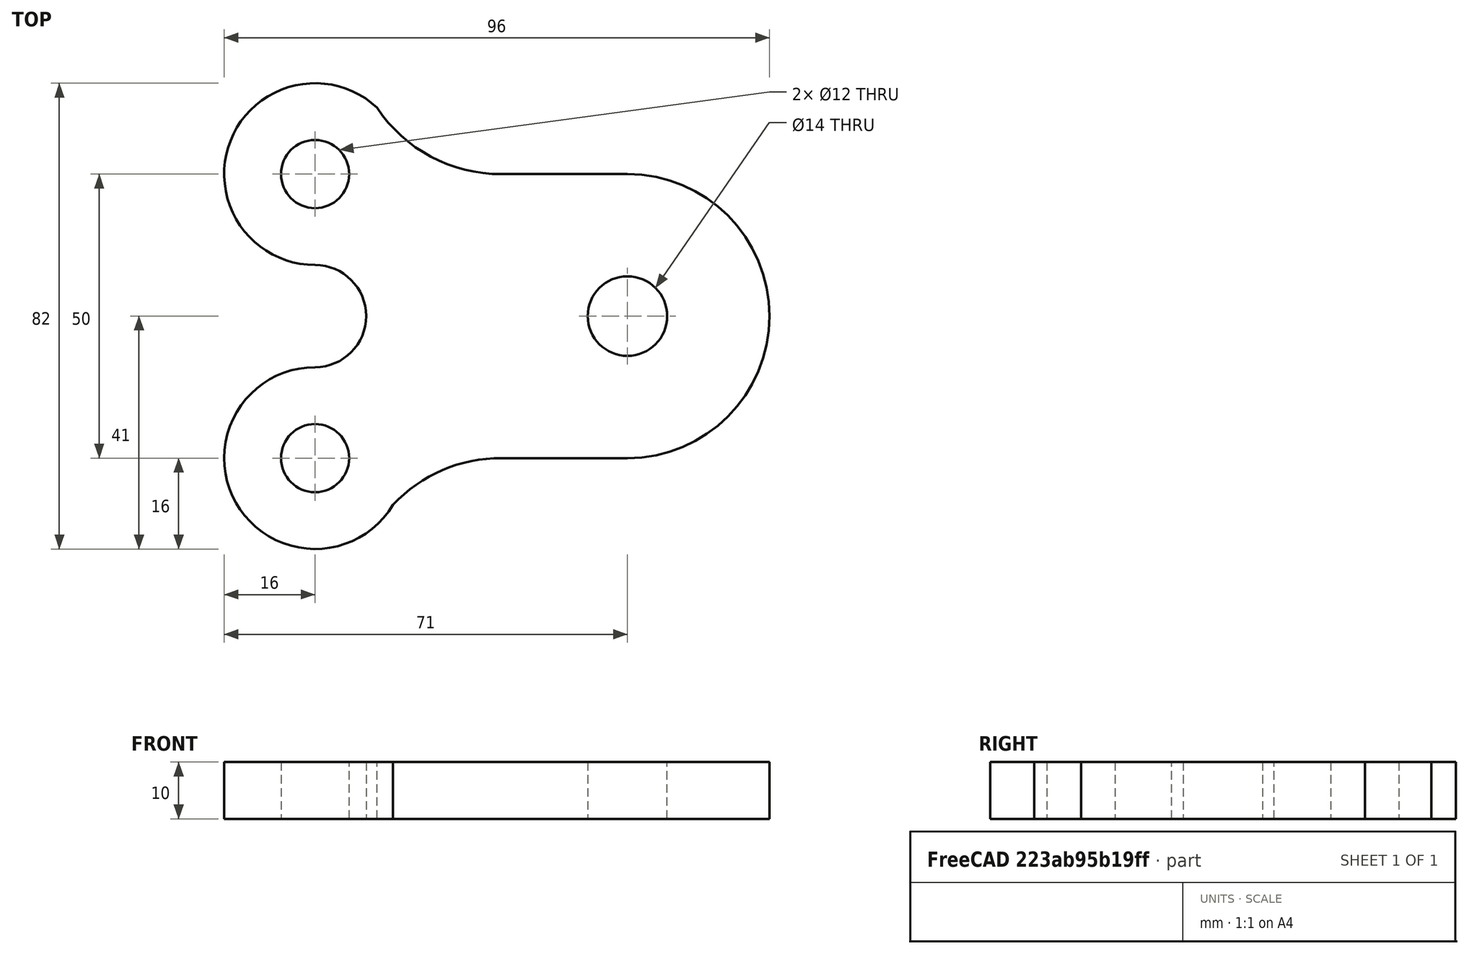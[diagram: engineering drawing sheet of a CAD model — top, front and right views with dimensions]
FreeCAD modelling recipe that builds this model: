
FCSTD DOCUMENT  (FreeCAD 0.18R4 (GitTag))
Label: Template 3 D39
License: All rights reserved
LicenseURL: http://en.wikipedia.org/wiki/All_rights_reserved
objects: TechDraw::DrawViewDimension×21, TechDraw::DrawProjGroupItem×8, TechDraw::DrawProjGroup×5, TechDraw::DrawViewAnnotation×4, TechDraw::DrawSVGTemplate×3, TechDraw::DrawPage×3, Sketcher::SketchObject×1, PartDesign::Pad×1, PartDesign::Body×1
note: 4 computed .brp shape members not serialized (recipe doc carries the construction recipe); baked Part::Feature solids carry a one-line shape summary decoded from their .brp

FEATURE [Sketcher::SketchObject] Sketch
  MapMode = 5
  Support = -> [XY_Plane]
  constraints (32):
    c: Perpendicular(g1,g-2) = 4.71239
    c: Perpendicular(g0,g-2) = 4.71239
    c: Coincident(g2,g0)
    c: Coincident(g2,g1)
    c: Radius(g2) = 25
    c: Coincident(g2,g-1)
    c: Coincident(g3,g2)
    c: Diameter(g3) = 14
    c: DistanceY(g5,g4) = 50
    c: Diameter(g4) = 12
    c: Diameter(g5) = 12
    c: Coincident(g6,g4)
    c: Coincident(g7,g5)
    c: Radius(g6) = 16
    c: Radius(g7) = 16
    c: PointOnObject(g8,g-1)
    c: Coincident(g8,g6)
    c: Coincident(g8,g7)
    c: Radius(g8) = 9
    c: Distance(g4,g0) = 55
    c: Distance(g5,g1) = 55
    c: DistanceX(g-2,g6) = -55
    c: DistanceX(g-2,g7) = -55
    c: Distance(g0,g1) = 50
    c: Coincident(g10,g0)
    c: Coincident(g10,g6)
    c: Coincident(g1,g9)
    c: Coincident(g9,g7)
    c: Radius(g10) = 26
    c: Radius(g9) = 26
    c: DistanceX(g0,g0) = 22.18
    c: DistanceY(g7,g6) = 69.89
FEATURE [PartDesign::Pad] Pad
  Length = 10
  Length2 = 100
  Profile = -> Sketch
  Type = 0
FEATURE [PartDesign::Body] Body
  Group = -> [Sketch,Pad]
  Origin = -> Origin
  Tip = -> Pad
FEATURE [TechDraw::DrawSVGTemplate] Template
  EditableTexts = Designed_by_Name=D 39; Drawing_number=AOT; FC-Date=19/12/2021; FC-SC=Scale; FC-SH=Sheet; FC-Title=Template 3; Subtitle=AKASHDIP MAHAPATRA; Weight=Weight
  Height = 210
  Orientation = 1
  Width = 297
FEATURE [TechDraw::DrawProjGroupItem] ProjItem  label="Front"
  CoarseView = false
  Direction = (0.41,-0.709,0.574)
  Focus = 100
  HardHidden = false
  IsoCount = 0
  IsoHidden = false
  IsoVisible = false
  LockPosition = true
  Perspective = false
  Rotation = 0
  RotationVector = (0.866,0.5,0)
  ScaleType = 2
  SeamHidden = false
  SeamVisible = true
  SmoothHidden = false
  SmoothVisible = true
  Source = -> [Pad]
  Type = 0
  X = 0
  Y = 0
FEATURE [TechDraw::DrawProjGroup] ProjGroup
  Anchor = -> ProjItem
  AutoDistribute = true
  LockPosition = false
  ProjectionType = 0
  Rotation = 0
  ScaleType = 0
  Source = -> [Pad]
  Views = -> [ProjItem]
  X = 0
  Y = 0
  spacingX = 15
  spacingY = 15
FEATURE [TechDraw::DrawProjGroupItem] ProjItem001  label="Front001"
  CoarseView = false
  Direction = (0,0,1)
  Focus = 100
  HardHidden = false
  IsoCount = 0
  IsoHidden = false
  IsoVisible = false
  LockPosition = true
  Perspective = false
  Rotation = 0
  RotationVector = (1,0,0)
  ScaleType = 2
  SeamHidden = false
  SeamVisible = true
  SmoothHidden = false
  SmoothVisible = true
  Source = -> [Pad]
  Type = 0
  X = 0
  Y = 0
FEATURE [TechDraw::DrawProjGroupItem] ProjItem002  label="Bottom"
  CoarseView = false
  Direction = (0,-1,0)
  Focus = 100
  HardHidden = false
  IsoCount = 0
  IsoHidden = false
  IsoVisible = false
  LockPosition = false
  Perspective = false
  Rotation = 0
  RotationVector = (1,0,0)
  ScaleType = 2
  SeamHidden = false
  SeamVisible = true
  SmoothHidden = false
  SmoothVisible = true
  Source = -> [Pad]
  Type = 5
  X = 0
  Y = 97
FEATURE [TechDraw::DrawProjGroupItem] ProjItem004  label="Right"
  CoarseView = false
  Direction = (1,0,1e-16)
  Focus = 100
  HardHidden = false
  IsoCount = 0
  IsoHidden = false
  IsoVisible = false
  LockPosition = false
  Perspective = false
  Rotation = 0
  RotationVector = (1,0,0)
  ScaleType = 2
  SeamHidden = false
  SeamVisible = true
  SmoothHidden = false
  SmoothVisible = true
  Source = -> [Pad]
  Type = 2
  X = 0
  Y = 0
FEATURE [TechDraw::DrawProjGroupItem] ProjItem005  label="Left"
  CoarseView = false
  Direction = (-1,0,1e-16)
  Focus = 100
  HardHidden = false
  IsoCount = 0
  IsoHidden = false
  IsoVisible = false
  LockPosition = false
  Perspective = false
  Rotation = 0
  RotationVector = (1,0,0)
  ScaleType = 2
  SeamHidden = false
  SeamVisible = true
  SmoothHidden = false
  SmoothVisible = true
  Source = -> [Pad]
  Type = 1
  X = 0
  Y = 0
FEATURE [TechDraw::DrawProjGroup] ProjGroup001
  Anchor = -> ProjItem001
  AutoDistribute = true
  LockPosition = false
  ProjectionType = 0
  Rotation = 0
  ScaleType = 0
  Source = -> [Pad]
  Views = -> [ProjItem001,ProjItem002,ProjItem004,ProjItem005]
  X = 0
  Y = 0
  spacingX = 15
  spacingY = 15
FEATURE [TechDraw::DrawViewDimension] Dimension
  Arbitrary = false
  FormatSpec = R%.2f
  LockPosition = false
  MeasureType = 1
  OverTolerance = 0
  References2D = -> [ProjItem001]
  Rotation = 0
  ScaleType = 0
  Type = 4
  UnderTolerance = 0
  X = 0
  Y = 0
FEATURE [TechDraw::DrawViewDimension] Dimension001
  Arbitrary = false
  FormatSpec = R%.2f
  LockPosition = false
  MeasureType = 1
  OverTolerance = 0
  References2D = -> [ProjItem001]
  Rotation = 0
  ScaleType = 0
  Type = 4
  UnderTolerance = 0
  X = 0
  Y = 0
FEATURE [TechDraw::DrawViewDimension] Dimension002
  Arbitrary = false
  FormatSpec = ⌀%.2f
  LockPosition = false
  MeasureType = 1
  OverTolerance = 0
  References2D = -> [ProjItem001]
  Rotation = 0
  ScaleType = 0
  Type = 5
  UnderTolerance = 0
  X = 0
  Y = 0
FEATURE [TechDraw::DrawViewDimension] Dimension003
  Arbitrary = false
  FormatSpec = R%.2f
  LockPosition = false
  MeasureType = 1
  OverTolerance = 0
  References2D = -> [ProjItem001]
  Rotation = 0
  ScaleType = 0
  Type = 4
  UnderTolerance = 0
  X = 0
  Y = 0
FEATURE [TechDraw::DrawViewDimension] Dimension004
  Arbitrary = false
  FormatSpec = ⌀%.2f
  LockPosition = false
  MeasureType = 1
  OverTolerance = 0
  References2D = -> [ProjItem001]
  Rotation = 0
  ScaleType = 0
  Type = 5
  UnderTolerance = 0
  X = 0
  Y = 0
FEATURE [TechDraw::DrawViewDimension] Dimension005
  Arbitrary = false
  FormatSpec = R%.2f
  LockPosition = false
  MeasureType = 1
  OverTolerance = 0
  References2D = -> [ProjItem001]
  Rotation = 0
  ScaleType = 0
  Type = 4
  UnderTolerance = 0
  X = 0
  Y = 0
FEATURE [TechDraw::DrawViewDimension] Dimension006
  Arbitrary = false
  FormatSpec = %.2f
  LockPosition = false
  MeasureType = 1
  OverTolerance = 0
  References2D = -> [ProjItem001]
  Rotation = 0
  ScaleType = 0
  Type = 2
  UnderTolerance = 0
  X = 0
  Y = 0
FEATURE [TechDraw::DrawViewDimension] Dimension007
  Arbitrary = false
  FormatSpec = %.2f
  LockPosition = false
  MeasureType = 1
  OverTolerance = 0
  References2D = -> [ProjItem004]
  Rotation = 0
  ScaleType = 0
  Type = 2
  UnderTolerance = 0
  X = 0
  Y = 0
FEATURE [TechDraw::DrawViewDimension] Dimension009
  Arbitrary = false
  FormatSpec = %.2f
  LockPosition = false
  MeasureType = 1
  OverTolerance = 0
  References2D = -> [ProjItem005]
  Rotation = 0
  ScaleType = 0
  Type = 2
  UnderTolerance = 0
  X = 0
  Y = 0
FEATURE [TechDraw::DrawViewDimension] Dimension010
  Arbitrary = false
  FormatSpec = %.2f
  LockPosition = false
  MeasureType = 1
  OverTolerance = 0
  References2D = -> [ProjItem005]
  Rotation = 0
  ScaleType = 0
  Type = 2
  UnderTolerance = 0
  X = 0
  Y = 0
FEATURE [TechDraw::DrawPage] Page
  KeepUpdated = true
  ProjectionType = 0
  Template = -> Template
  Views = -> [ProjGroup,ProjGroup001,Dimension,Dimension001,Dimension002,Dimension003,Dimension004,Dimension005,Dimension006,Dimension007,Dimension009,Dimension010]
FEATURE [TechDraw::DrawSVGTemplate] Template001
  EditableTexts = Designed_by_Name=SOUMOJIT SHOME; Drawing_number=Drawing number; FC-SC=1 : 1; FC-Title=ACADEMY OF TECHNOLOGY; Subtitle=ECE - 3 (X) ROLL - 139; Weight=Weight
  Height = 210
  Orientation = 1
  Width = 297
FEATURE [TechDraw::DrawSVGTemplate] Template002
  EditableTexts = Designed_by_Name=Designed by Name; Drawing_number=Drawing number; FC-Date=Date; FC-SC=Scale; FC-SH=Sheet; FC-Title=Title; Subtitle=Subtitle; Weight=Weight
  Height = 210
  Orientation = 1
  Width = 297
FEATURE [TechDraw::DrawPage] Page002
  KeepUpdated = true
  ProjectionType = 0
  Template = -> Template002
FEATURE [TechDraw::DrawProjGroupItem] ProjItem006  label="Front002"
  CoarseView = false
  Direction = (0.577,-0.577,0.577)
  Focus = 100
  HardHidden = false
  IsoCount = 0
  IsoHidden = false
  IsoVisible = false
  LockPosition = true
  Perspective = false
  Rotation = 0
  RotationVector = (0.707,0.707,0)
  ScaleType = 2
  SeamHidden = false
  SeamVisible = false
  SmoothHidden = false
  SmoothVisible = false
  Source = -> [Pad]
  Type = 0
  X = 0
  Y = 0
FEATURE [TechDraw::DrawProjGroup] ProjGroup002
  Anchor = -> ProjItem006
  AutoDistribute = true
  LockPosition = false
  ProjectionType = 0
  Rotation = 0
  ScaleType = 0
  Source = -> [Pad]
  Views = -> [ProjItem006]
  X = 225.272
  Y = 132.391
  spacingX = 15
  spacingY = 15
FEATURE [TechDraw::DrawProjGroupItem] ProjItem007  label="Front003"
  CoarseView = false
  Direction = (0,-1,0)
  Focus = 100
  HardHidden = false
  IsoCount = 0
  IsoHidden = false
  IsoVisible = false
  LockPosition = true
  Perspective = false
  Rotation = 0
  RotationVector = (1,0,0)
  ScaleType = 2
  SeamHidden = false
  SeamVisible = false
  SmoothHidden = false
  SmoothVisible = false
  Source = -> [Pad]
  Type = 0
  X = 0
  Y = 0
FEATURE [TechDraw::DrawProjGroup] ProjGroup003
  Anchor = -> ProjItem007
  AutoDistribute = true
  LockPosition = false
  ProjectionType = 0
  Rotation = 0
  ScaleType = 0
  Source = -> [Pad]
  Views = -> [ProjItem007]
  X = 79.6086
  Y = 180.917
  spacingX = 15
  spacingY = 15
FEATURE [TechDraw::DrawProjGroupItem] ProjItem008  label="Front004"
  CoarseView = false
  Direction = (0,0,1)
  Focus = 100
  HardHidden = false
  IsoCount = 0
  IsoHidden = false
  IsoVisible = false
  LockPosition = true
  Perspective = false
  Rotation = 0
  RotationVector = (1,0,0)
  ScaleType = 2
  SeamHidden = false
  SeamVisible = false
  SmoothHidden = false
  SmoothVisible = false
  Source = -> [Pad]
  Type = 0
  X = 0
  Y = 0
FEATURE [TechDraw::DrawProjGroup] ProjGroup004
  Anchor = -> ProjItem008
  AutoDistribute = true
  LockPosition = false
  ProjectionType = 0
  Rotation = 0
  ScaleType = 0
  Source = -> [Pad]
  Views = -> [ProjItem008]
  X = 84.1663
  Y = 83.3944
  spacingX = 15
  spacingY = 15
FEATURE [TechDraw::DrawViewAnnotation] Annotation
  Font = osifont
  LineSpace = 80
  LockPosition = false
  MaxWidth = -1
  Rotation = 0
  ScaleType = 0
  Text = Isometric View
  TextSize = 6
  TextStyle = 0
  X = 228.09
  Y = 81.7589
FEATURE [TechDraw::DrawViewAnnotation] Annotation001
  Font = osifont
  LineSpace = 80
  LockPosition = false
  MaxWidth = -1
  Rotation = 0
  ScaleType = 0
  Text = Front View
  TextSize = 6
  TextStyle = 0
  X = 82.4986
  Y = 160.15
FEATURE [TechDraw::DrawViewAnnotation] Annotation002
  Font = osifont
  LineSpace = 80
  LockPosition = false
  MaxWidth = -1
  Rotation = 0
  ScaleType = 0
  Text = Top View
  TextSize = 6
  TextStyle = 0
  X = 87.0714
  Y = 36.9217
FEATURE [TechDraw::DrawViewDimension] Dimension011
  Arbitrary = false
  FormatSpec = ⌀%.2f
  LockPosition = false
  MeasureType = 1
  OverTolerance = 0
  References2D = -> [ProjItem008]
  Rotation = 0
  ScaleType = 0
  Type = 5
  UnderTolerance = 0
  X = 68.0879
  Y = 33.9598
FEATURE [TechDraw::DrawViewDimension] Dimension012
  Arbitrary = false
  FormatSpec = R%.2f
  LockPosition = false
  MeasureType = 1
  OverTolerance = 0
  References2D = -> [ProjItem008]
  Rotation = 0
  ScaleType = 0
  Type = 4
  UnderTolerance = 0
  X = 79.2688
  Y = 7.05534
FEATURE [TechDraw::DrawViewDimension] Dimension013
  Arbitrary = false
  FormatSpec = %.2f
  LockPosition = false
  MeasureType = 1
  OverTolerance = 0
  References2D = -> [ProjItem008]
  Rotation = 0
  ScaleType = 0
  Type = 2
  UnderTolerance = 0
  X = 53.5275
  Y = -9.96047
FEATURE [TechDraw::DrawViewDimension] Dimension014
  Arbitrary = false
  FormatSpec = R%.2f
  LockPosition = false
  MeasureType = 1
  OverTolerance = 0
  References2D = -> [ProjItem008]
  Rotation = 0
  ScaleType = 0
  Type = 4
  UnderTolerance = 0
  X = 67.1883
  Y = 42.6752
FEATURE [TechDraw::DrawViewDimension] Dimension015
  Arbitrary = false
  FormatSpec = %.2f
  LockPosition = false
  MeasureType = 1
  OverTolerance = 0
  References2D = -> [ProjItem008]
  Rotation = 0
  ScaleType = 0
  Type = 1
  UnderTolerance = 0
  X = -8.13872
  Y = 60.8128
FEATURE [TechDraw::DrawViewDimension] Dimension016
  Arbitrary = false
  FormatSpec = R%.2f
  LockPosition = false
  MeasureType = 1
  OverTolerance = 0
  References2D = -> [ProjItem008]
  Rotation = 0
  ScaleType = 0
  Type = 4
  UnderTolerance = 0
  X = -60.1779
  Y = 43.5367
FEATURE [TechDraw::DrawViewDimension] Dimension017
  Arbitrary = false
  FormatSpec = R%.2f
  LockPosition = false
  MeasureType = 1
  OverTolerance = 0
  References2D = -> [ProjItem008]
  Rotation = 0
  ScaleType = 0
  Type = 4
  UnderTolerance = 0
  X = -53.5375
  Y = -6.6964
FEATURE [TechDraw::DrawViewDimension] Dimension018
  Arbitrary = false
  FormatSpec = %.2f
  LockPosition = false
  MeasureType = 1
  OverTolerance = 0
  References2D = -> [ProjItem008]
  Rotation = 0
  ScaleType = 0
  Type = 2
  UnderTolerance = 0
  X = -55.1324
  Y = 12.915
FEATURE [TechDraw::DrawViewDimension] Dimension019
  Arbitrary = false
  FormatSpec = %.2f
  LockPosition = false
  MeasureType = 1
  OverTolerance = 0
  References2D = -> [ProjItem008]
  Rotation = 0
  ScaleType = 0
  Type = 2
  UnderTolerance = 0
  X = -68.9368
  Y = -3.32016
FEATURE [TechDraw::DrawViewDimension] Dimension020
  Arbitrary = false
  FormatSpec = ⌀%.2f
  LockPosition = false
  MeasureType = 1
  OverTolerance = 0
  References2D = -> [ProjItem008]
  Rotation = 0
  ScaleType = 0
  Type = 5
  UnderTolerance = 0
  X = -59.6754
  Y = -43.6578
FEATURE [TechDraw::DrawViewDimension] Dimension021
  Arbitrary = false
  FormatSpec = %.2f
  LockPosition = false
  MeasureType = 1
  OverTolerance = 0
  References2D = -> [ProjItem007]
  Rotation = 0
  ScaleType = 0
  Type = 2
  UnderTolerance = 0
  X = 56.7154
  Y = -15.7708
FEATURE [TechDraw::DrawViewAnnotation] Annotation003
  Font = osifont
  LineSpace = 80
  LockPosition = false
  MaxWidth = -1
  Rotation = 0
  ScaleType = 0
  Text = Template 3
  TextSize = 5
  TextStyle = 0
  X = 203.86
  Y = 32.2887
FEATURE [TechDraw::DrawPage] Page001
  KeepUpdated = true
  ProjectionType = 0
  Template = -> Template001
  Views = -> [ProjGroup002,ProjGroup003,ProjGroup004,Annotation,Annotation001,Annotation002,Dimension011,Dimension012,Dimension013,Dimension014,Dimension015,Dimension016,Dimension017,Dimension018,Dimension019,Dimension020,Dimension021,Annotation003]
